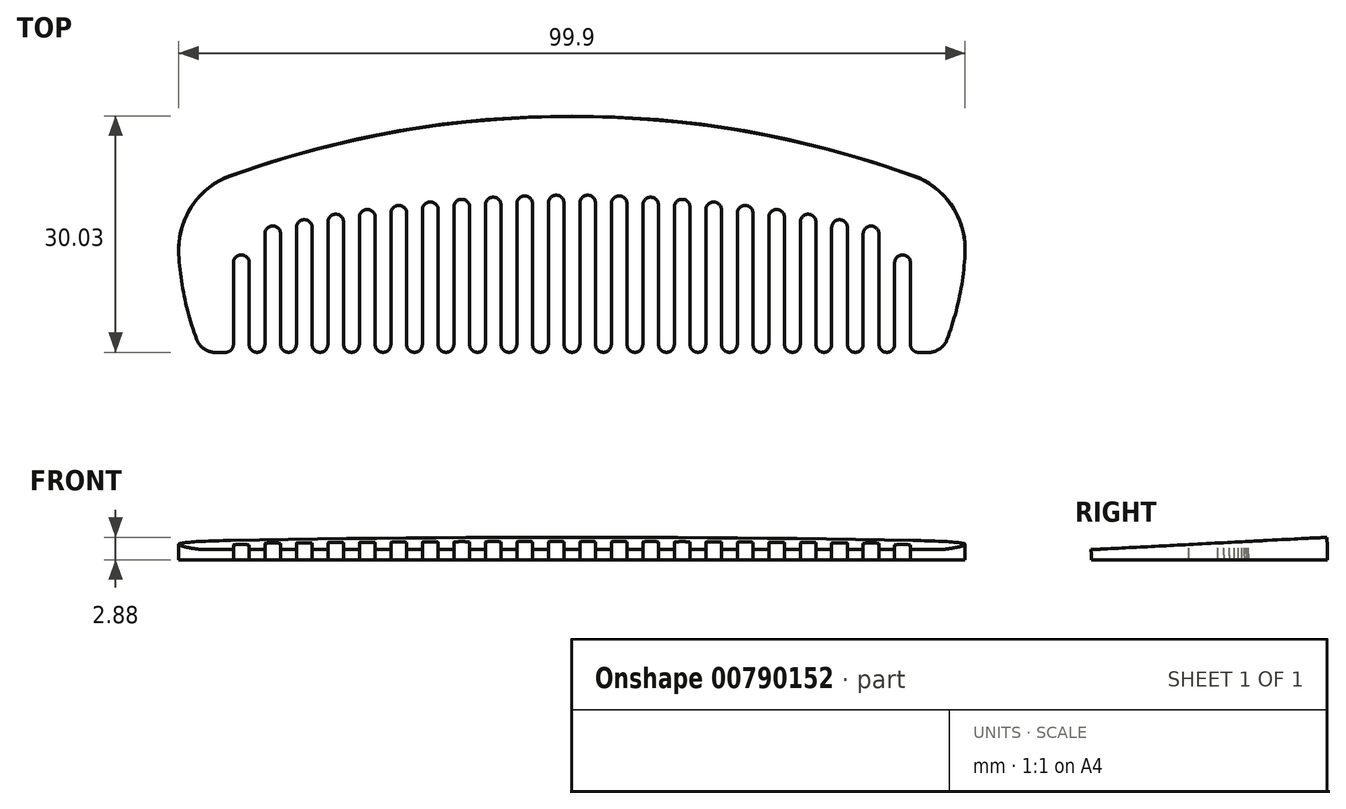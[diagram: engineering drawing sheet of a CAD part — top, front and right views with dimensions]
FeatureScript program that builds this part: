
annotation { "Feature Type Name" : "Feature", "Feature Type Description" : "" }
export const myFeature = defineFeature(function(context is Context, id is Id, definition is map)
    precondition{}
    {
        {
            var Q0;
            Q0=qCreatedBy(makeId("Top.planeOp"),FACE);
            var sketch = newSketch(context, id + "F0", { "sketchPlane" : qUnion([Q0])});
            skArc(sketch, "E0", {"start": v(-43.34, -7.56) * mm, "mid": v(-48.3, -11.46) * mm, "end": v(-49.94, -17.55) * mm});
            skArc(sketch, "E1", {"start": v(-49.94, -17.55) * mm, "mid": v(-49.01, -23.9) * mm, "end": v(-47, -30) * mm});
            skLineSegment(sketch, "E2", {"start": v(-47, -30) * mm, "end": v(-43, -30) * mm});
            skLineSegment(sketch, "E3", {"start": v(-43, -30) * mm, "end": v(-43, -18.6) * mm});
            skLineSegment(sketch, "E4", {"start": v(0, 0) * mm, "end": v(0, -30) * mm});
            skPoint(sketch, "E5", {"position": v(0, -10) * mm});
            skLineSegment(sketch, "E6", {"start": v(-41, -10) * mm, "end": v(-41, -30) * mm});
            skLineSegment(sketch, "E7", {"start": v(-41, -30) * mm, "end": v(-39, -30) * mm});
            skLineSegment(sketch, "E8", {"start": v(-39, -30) * mm, "end": v(-39, -10) * mm});
            skLineSegment(sketch, "E9", {"start": v(-39, -30) * mm, "end": v(-37, -30) * mm, "construction": true});
            skLineSegment(sketch, "E10", {"start": v(-43, -30) * mm, "end": v(-41, -30) * mm, "construction": true});
            skLineSegment(sketch, "E11", {"start": v(-47, -55) * mm, "end": v(0, -55) * mm, "construction": true});
            skArc(sketch, "E12", {"start": v(0, -10) * mm, "mid": v(-19.84, -11.05) * mm, "end": v(-39.45, -14.2) * mm});
            skLineSegment(sketch, "E13.1.0.0", {"start": v(-37, -10) * mm, "end": v(-37, -30) * mm});
            skLineSegment(sketch, "E13.1.0.1", {"start": v(-37, -30) * mm, "end": v(-35, -30) * mm});
            skLineSegment(sketch, "E13.1.0.2", {"start": v(-35, -30) * mm, "end": v(-35, -10) * mm});
            skLineSegment(sketch, "E13.1.0.3", {"start": v(-35, -30) * mm, "end": v(-33, -30) * mm, "construction": true});
            skLineSegment(sketch, "E13.2.0.0", {"start": v(-33, -10) * mm, "end": v(-33, -30) * mm});
            skLineSegment(sketch, "E13.2.0.1", {"start": v(-33, -30) * mm, "end": v(-31, -30) * mm});
            skLineSegment(sketch, "E13.2.0.2", {"start": v(-31, -30) * mm, "end": v(-31, -10) * mm});
            skLineSegment(sketch, "E13.2.0.3", {"start": v(-31, -30) * mm, "end": v(-29, -30) * mm, "construction": true});
            skLineSegment(sketch, "E13.direction1", {"start": v(-41, -30) * mm, "end": v(-37, -30) * mm, "construction": true});
            skLineSegment(sketch, "E14.0.3.0", {"start": v(-29, -10) * mm, "end": v(-29, -30) * mm});
            skLineSegment(sketch, "E14.3.3.0", {"start": v(-29, -30) * mm, "end": v(-27, -30) * mm});
            skLineSegment(sketch, "E14.6.3.0", {"start": v(-27, -30) * mm, "end": v(-27, -10) * mm});
            skLineSegment(sketch, "E14.9.3.0", {"start": v(-27, -30) * mm, "end": v(-25, -30) * mm, "construction": true});
            skLineSegment(sketch, "E14.0.4.0", {"start": v(-25, -10) * mm, "end": v(-25, -30) * mm});
            skLineSegment(sketch, "E14.3.4.0", {"start": v(-25, -30) * mm, "end": v(-23, -30) * mm});
            skLineSegment(sketch, "E14.6.4.0", {"start": v(-23, -30) * mm, "end": v(-23, -10) * mm});
            skLineSegment(sketch, "E14.9.4.0", {"start": v(-23, -30) * mm, "end": v(-21, -30) * mm, "construction": true});
            skLineSegment(sketch, "E14.0.5.0", {"start": v(-21, -10) * mm, "end": v(-21, -30) * mm});
            skLineSegment(sketch, "E14.3.5.0", {"start": v(-21, -30) * mm, "end": v(-19, -30) * mm});
            skLineSegment(sketch, "E14.6.5.0", {"start": v(-19, -30) * mm, "end": v(-19, -10) * mm});
            skLineSegment(sketch, "E14.9.5.0", {"start": v(-19, -30) * mm, "end": v(-17, -30) * mm, "construction": true});
            skLineSegment(sketch, "E14.0.6.0", {"start": v(-17, -10) * mm, "end": v(-17, -30) * mm});
            skLineSegment(sketch, "E14.3.6.0", {"start": v(-17, -30) * mm, "end": v(-15, -30) * mm});
            skLineSegment(sketch, "E14.6.6.0", {"start": v(-15, -30) * mm, "end": v(-15, -10) * mm});
            skLineSegment(sketch, "E14.9.6.0", {"start": v(-15, -30) * mm, "end": v(-13, -30) * mm, "construction": true});
            skLineSegment(sketch, "E14.0.7.0", {"start": v(-13, -10) * mm, "end": v(-13, -30) * mm});
            skLineSegment(sketch, "E14.3.7.0", {"start": v(-13, -30) * mm, "end": v(-11, -30) * mm});
            skLineSegment(sketch, "E14.6.7.0", {"start": v(-11, -30) * mm, "end": v(-11, -10) * mm});
            skLineSegment(sketch, "E14.9.7.0", {"start": v(-11, -30) * mm, "end": v(-9, -30) * mm, "construction": true});
            skLineSegment(sketch, "E14.0.8.0", {"start": v(-9, -10) * mm, "end": v(-9, -30) * mm});
            skLineSegment(sketch, "E14.3.8.0", {"start": v(-9, -30) * mm, "end": v(-7, -30) * mm});
            skLineSegment(sketch, "E14.6.8.0", {"start": v(-7, -30) * mm, "end": v(-7, -10) * mm});
            skLineSegment(sketch, "E14.9.8.0", {"start": v(-7, -30) * mm, "end": v(-5, -30) * mm, "construction": true});
            skLineSegment(sketch, "E14.0.9.0", {"start": v(-5, -10) * mm, "end": v(-5, -30) * mm});
            skLineSegment(sketch, "E14.3.9.0", {"start": v(-5, -30) * mm, "end": v(-3, -30) * mm});
            skLineSegment(sketch, "E14.6.9.0", {"start": v(-3, -30) * mm, "end": v(-3, -10) * mm});
            skLineSegment(sketch, "E14.9.9.0", {"start": v(-3, -30) * mm, "end": v(-1, -30) * mm, "construction": true});
            skArc(sketch, "E15", {"start": v(0, 0) * mm, "mid": v(-22, -1.9) * mm, "end": v(-43.34, -7.56) * mm});
            skArc(sketch, "E16", {"start": v(-39.45, -14.2) * mm, "mid": v(-42, -15.77) * mm, "end": v(-43, -18.6) * mm});
            skArc(sketch, "E17", {"start": v(-43.34, -7.56) * mm, "mid": v(-46.49, -8.74) * mm, "end": v(-49.6, -10) * mm, "construction": true});
            skArc(sketch, "E18", {"start": v(-49.6, -10) * mm, "mid": v(-49.96, -13.77) * mm, "end": v(-49.94, -17.55) * mm, "construction": true});
            skLineSegment(sketch, "E19", {"start": v(-43, -18.6) * mm, "end": v(-43, -15) * mm, "construction": true});
            skLineSegment(sketch, "E20", {"start": v(-50, 0) * mm, "end": v(-50, -30) * mm, "construction": true});
            skArc(sketch, "E21", {"start": v(-39.45, -14.2) * mm, "mid": v(-41.23, -14.6) * mm, "end": v(-43, -15) * mm, "construction": true});
            skLineSegment(sketch, "E22", {"start": v(0, -10) * mm, "end": v(-50, -10) * mm, "construction": true});
            skLineSegment(sketch, "E23", {"start": v(-50, 0) * mm, "end": v(0, 0) * mm, "construction": true});
            skLineSegment(sketch, "E24.0.10.0", {"start": v(-1, -10) * mm, "end": v(-1, -30) * mm});
            skLineSegment(sketch, "E24.3.10.0", {"start": v(-1, -30) * mm, "end": v(1, -30) * mm});
            skLineSegment(sketch, "E24.6.10.0", {"start": v(1, -30) * mm, "end": v(1, -10) * mm});
            skLineSegment(sketch, "E24.9.10.0", {"start": v(1, -30) * mm, "end": v(3, -30) * mm, "construction": true});
            skSolve(sketch);
        }
        {
            var Q0;
            Q0 = qSketchRegion(id + "F0", true);
            var Q1;
            Q1=sQuery(id+"F0.wireOp",EDGE,"E11");
            revolve(context, id + "F1", {"surfaceOperationType" : NewSurfaceOperationType.NEW, "entities" : qUnion([Q0]), "axis" : qUnion([Q1]), "revolveType" : RevolveType.ONE_DIRECTION, "angle" : 3 * degree});
        }
        {
            var Q0;
            Q0=makeQuery(id+"F1.opRevolve","SWEPT_EDGE",EDGE,{"disambiguationData":[OSD([sQuery(id+"F0.wireOp",EDGE,"E3"),sQuery(id+"F0.wireOp",EDGE,"E16")])]});
            var Q1;
            Q1=makeQuery(id+"F1.opRevolve","SWEPT_EDGE",EDGE,{"disambiguationData":[OSD([sQuery(id+"F0.wireOp",EDGE,"E6"),sQuery(id+"F0.wireOp",EDGE,"E16")])]});
            var Q2;
            Q2=makeQuery(id+"F1.opRevolve","SWEPT_EDGE",EDGE,{"disambiguationData":[OSD([sQuery(id+"F0.wireOp",EDGE,"E12"),sQuery(id+"F0.wireOp",EDGE,"E13.1.0.0")])]});
            var Q3;
            Q3=makeQuery(id+"F1.opRevolve","SWEPT_EDGE",EDGE,{"disambiguationData":[OSD([sQuery(id+"F0.wireOp",EDGE,"E8"),sQuery(id+"F0.wireOp",EDGE,"E12")])]});
            var Q4;
            Q4=makeQuery(id+"F1.opRevolve","SWEPT_EDGE",EDGE,{"disambiguationData":[OSD([sQuery(id+"F0.wireOp",EDGE,"E12"),sQuery(id+"F0.wireOp",EDGE,"E24.0.10.0")])]});
            var Q5;
            Q5=makeQuery(id+"F1.opRevolve","SWEPT_EDGE",EDGE,{"disambiguationData":[OSD([sQuery(id+"F0.wireOp",EDGE,"E12"),sQuery(id+"F0.wireOp",EDGE,"E14.6.9.0")])]});
            var Q6;
            Q6=makeQuery(id+"F1.opRevolve","SWEPT_EDGE",EDGE,{"disambiguationData":[OSD([sQuery(id+"F0.wireOp",EDGE,"E12"),sQuery(id+"F0.wireOp",EDGE,"E14.0.9.0")])]});
            var Q7;
            Q7=makeQuery(id+"F1.opRevolve","SWEPT_EDGE",EDGE,{"disambiguationData":[OSD([sQuery(id+"F0.wireOp",EDGE,"E12"),sQuery(id+"F0.wireOp",EDGE,"E14.6.8.0")])]});
            var Q8;
            Q8=makeQuery(id+"F1.opRevolve","SWEPT_EDGE",EDGE,{"disambiguationData":[OSD([sQuery(id+"F0.wireOp",EDGE,"E12"),sQuery(id+"F0.wireOp",EDGE,"E14.0.8.0")])]});
            var Q9;
            Q9=makeQuery(id+"F1.opRevolve","SWEPT_EDGE",EDGE,{"disambiguationData":[OSD([sQuery(id+"F0.wireOp",EDGE,"E12"),sQuery(id+"F0.wireOp",EDGE,"E14.6.7.0")])]});
            var Q10;
            Q10=makeQuery(id+"F1.opRevolve","SWEPT_EDGE",EDGE,{"disambiguationData":[OSD([sQuery(id+"F0.wireOp",EDGE,"E12"),sQuery(id+"F0.wireOp",EDGE,"E14.0.7.0")])]});
            var Q11;
            Q11=makeQuery(id+"F1.opRevolve","SWEPT_EDGE",EDGE,{"disambiguationData":[OSD([sQuery(id+"F0.wireOp",EDGE,"E12"),sQuery(id+"F0.wireOp",EDGE,"E14.6.6.0")])]});
            var Q12;
            Q12=makeQuery(id+"F1.opRevolve","SWEPT_EDGE",EDGE,{"disambiguationData":[OSD([sQuery(id+"F0.wireOp",EDGE,"E12"),sQuery(id+"F0.wireOp",EDGE,"E14.0.6.0")])]});
            var Q13;
            Q13=makeQuery(id+"F1.opRevolve","SWEPT_EDGE",EDGE,{"disambiguationData":[OSD([sQuery(id+"F0.wireOp",EDGE,"E12"),sQuery(id+"F0.wireOp",EDGE,"E14.6.5.0")])]});
            var Q14;
            Q14=makeQuery(id+"F1.opRevolve","SWEPT_EDGE",EDGE,{"disambiguationData":[OSD([sQuery(id+"F0.wireOp",EDGE,"E12"),sQuery(id+"F0.wireOp",EDGE,"E14.0.5.0")])]});
            var Q15;
            Q15=makeQuery(id+"F1.opRevolve","SWEPT_EDGE",EDGE,{"disambiguationData":[OSD([sQuery(id+"F0.wireOp",EDGE,"E12"),sQuery(id+"F0.wireOp",EDGE,"E14.6.4.0")])]});
            var Q16;
            Q16=makeQuery(id+"F1.opRevolve","SWEPT_EDGE",EDGE,{"disambiguationData":[OSD([sQuery(id+"F0.wireOp",EDGE,"E12"),sQuery(id+"F0.wireOp",EDGE,"E14.0.4.0")])]});
            var Q17;
            Q17=makeQuery(id+"F1.opRevolve","SWEPT_EDGE",EDGE,{"disambiguationData":[OSD([sQuery(id+"F0.wireOp",EDGE,"E12"),sQuery(id+"F0.wireOp",EDGE,"E14.6.3.0")])]});
            var Q18;
            Q18=makeQuery(id+"F1.opRevolve","SWEPT_EDGE",EDGE,{"disambiguationData":[OSD([sQuery(id+"F0.wireOp",EDGE,"E12"),sQuery(id+"F0.wireOp",EDGE,"E14.0.3.0")])]});
            var Q19;
            Q19=makeQuery(id+"F1.opRevolve","SWEPT_EDGE",EDGE,{"disambiguationData":[OSD([sQuery(id+"F0.wireOp",EDGE,"E12"),sQuery(id+"F0.wireOp",EDGE,"E13.2.0.2")])]});
            var Q20;
            Q20=makeQuery(id+"F1.opRevolve","SWEPT_EDGE",EDGE,{"disambiguationData":[OSD([sQuery(id+"F0.wireOp",EDGE,"E12"),sQuery(id+"F0.wireOp",EDGE,"E13.2.0.0")])]});
            var Q21;
            Q21=makeQuery(id+"F1.opRevolve","SWEPT_EDGE",EDGE,{"disambiguationData":[OSD([sQuery(id+"F0.wireOp",EDGE,"E12"),sQuery(id+"F0.wireOp",EDGE,"E13.1.0.2")])]});
            fillet(context, id + "F2", {"entities" : qUnion([Q0, Q1, Q2, Q3, Q4, Q5, Q6, Q7, Q8, Q9, Q10, Q11, Q12, Q13, Q14, Q15, Q16, Q17, Q18, Q19, Q20, Q21]), "radius" : 1 * mm, "tangentPropagation" : true, "allowEdgeOverflow" : false});
        }
        {
            var Q0;
            Q0=makeQuery(id+"F1.opRevolve","SWEPT_EDGE",EDGE,{"disambiguationData":[OSD([sQuery(id+"F0.wireOp",EDGE,"E14.0.20.0"),sQuery(id+"F0.wireOp",EDGE,"E14.3.20.0")])]});
            var Q1;
            Q1=makeQuery(id+"F1.opRevolve","SWEPT_EDGE",EDGE,{"disambiguationData":[OSD([sQuery(id+"F0.wireOp",EDGE,"E14.3.20.0"),sQuery(id+"F0.wireOp",EDGE,"E14.6.20.0")])]});
            var Q2;
            Q2=makeQuery(id+"F1.opRevolve","SWEPT_EDGE",EDGE,{"disambiguationData":[OSD([sQuery(id+"F0.wireOp",EDGE,"E14.3.19.0"),sQuery(id+"F0.wireOp",EDGE,"E14.6.19.0")])]});
            var Q3;
            Q3=makeQuery(id+"F1.opRevolve","SWEPT_EDGE",EDGE,{"disambiguationData":[OSD([sQuery(id+"F0.wireOp",EDGE,"E14.0.19.0"),sQuery(id+"F0.wireOp",EDGE,"E14.3.19.0")])]});
            var Q4;
            Q4=makeQuery(id+"F1.opRevolve","SWEPT_EDGE",EDGE,{"disambiguationData":[OSD([sQuery(id+"F0.wireOp",EDGE,"E14.3.18.0"),sQuery(id+"F0.wireOp",EDGE,"E14.6.18.0")])]});
            var Q5;
            Q5=makeQuery(id+"F1.opRevolve","SWEPT_EDGE",EDGE,{"disambiguationData":[OSD([sQuery(id+"F0.wireOp",EDGE,"E14.0.18.0"),sQuery(id+"F0.wireOp",EDGE,"E14.3.18.0")])]});
            var Q6;
            Q6=makeQuery(id+"F1.opRevolve","SWEPT_EDGE",EDGE,{"disambiguationData":[OSD([sQuery(id+"F0.wireOp",EDGE,"E14.3.17.0"),sQuery(id+"F0.wireOp",EDGE,"E14.6.17.0")])]});
            var Q7;
            Q7=makeQuery(id+"F1.opRevolve","SWEPT_EDGE",EDGE,{"disambiguationData":[OSD([sQuery(id+"F0.wireOp",EDGE,"E14.0.17.0"),sQuery(id+"F0.wireOp",EDGE,"E14.3.17.0")])]});
            var Q8;
            Q8=makeQuery(id+"F1.opRevolve","SWEPT_EDGE",EDGE,{"disambiguationData":[OSD([sQuery(id+"F0.wireOp",EDGE,"E14.3.16.0"),sQuery(id+"F0.wireOp",EDGE,"E14.6.16.0")])]});
            var Q9;
            Q9=makeQuery(id+"F1.opRevolve","SWEPT_EDGE",EDGE,{"disambiguationData":[OSD([sQuery(id+"F0.wireOp",EDGE,"E14.0.16.0"),sQuery(id+"F0.wireOp",EDGE,"E14.3.16.0")])]});
            var Q10;
            Q10=makeQuery(id+"F1.opRevolve","SWEPT_EDGE",EDGE,{"disambiguationData":[OSD([sQuery(id+"F0.wireOp",EDGE,"E14.3.15.0"),sQuery(id+"F0.wireOp",EDGE,"E14.6.15.0")])]});
            var Q11;
            Q11=makeQuery(id+"F1.opRevolve","SWEPT_EDGE",EDGE,{"disambiguationData":[OSD([sQuery(id+"F0.wireOp",EDGE,"E14.0.15.0"),sQuery(id+"F0.wireOp",EDGE,"E14.3.15.0")])]});
            var Q12;
            Q12=makeQuery(id+"F1.opRevolve","SWEPT_EDGE",EDGE,{"disambiguationData":[OSD([sQuery(id+"F0.wireOp",EDGE,"E14.3.14.0"),sQuery(id+"F0.wireOp",EDGE,"E14.6.14.0")])]});
            var Q13;
            Q13=makeQuery(id+"F1.opRevolve","SWEPT_EDGE",EDGE,{"disambiguationData":[OSD([sQuery(id+"F0.wireOp",EDGE,"E14.0.14.0"),sQuery(id+"F0.wireOp",EDGE,"E14.3.14.0")])]});
            var Q14;
            Q14=makeQuery(id+"F1.opRevolve","SWEPT_EDGE",EDGE,{"disambiguationData":[OSD([sQuery(id+"F0.wireOp",EDGE,"E14.3.13.0"),sQuery(id+"F0.wireOp",EDGE,"E14.6.13.0")])]});
            var Q15;
            Q15=makeQuery(id+"F1.opRevolve","SWEPT_EDGE",EDGE,{"disambiguationData":[OSD([sQuery(id+"F0.wireOp",EDGE,"E14.0.13.0"),sQuery(id+"F0.wireOp",EDGE,"E14.3.13.0")])]});
            var Q16;
            Q16=makeQuery(id+"F1.opRevolve","SWEPT_EDGE",EDGE,{"disambiguationData":[OSD([sQuery(id+"F0.wireOp",EDGE,"E14.3.12.0"),sQuery(id+"F0.wireOp",EDGE,"E14.6.12.0")])]});
            var Q17;
            Q17=makeQuery(id+"F1.opRevolve","SWEPT_EDGE",EDGE,{"disambiguationData":[OSD([sQuery(id+"F0.wireOp",EDGE,"E14.0.12.0"),sQuery(id+"F0.wireOp",EDGE,"E14.3.12.0")])]});
            var Q18;
            Q18=makeQuery(id+"F1.opRevolve","SWEPT_EDGE",EDGE,{"disambiguationData":[OSD([sQuery(id+"F0.wireOp",EDGE,"E14.3.11.0"),sQuery(id+"F0.wireOp",EDGE,"E14.6.11.0")])]});
            var Q19;
            Q19=makeQuery(id+"F1.opRevolve","SWEPT_EDGE",EDGE,{"disambiguationData":[OSD([sQuery(id+"F0.wireOp",EDGE,"E14.0.11.0"),sQuery(id+"F0.wireOp",EDGE,"E14.3.11.0")])]});
            var Q20;
            Q20=makeQuery(id+"F1.opRevolve","SWEPT_EDGE",EDGE,{"disambiguationData":[OSD([sQuery(id+"F0.wireOp",EDGE,"E14.3.10.0"),sQuery(id+"F0.wireOp",EDGE,"E14.6.10.0")])]});
            var Q21;
            Q21=makeQuery(id+"F1.opRevolve","SWEPT_EDGE",EDGE,{"disambiguationData":[OSD([sQuery(id+"F0.wireOp",EDGE,"E14.0.10.0"),sQuery(id+"F0.wireOp",EDGE,"E14.3.10.0")])]});
            var Q22;
            Q22=makeQuery(id+"F1.opRevolve","SWEPT_EDGE",EDGE,{"disambiguationData":[OSD([sQuery(id+"F0.wireOp",EDGE,"E14.3.9.0"),sQuery(id+"F0.wireOp",EDGE,"E14.6.9.0")])]});
            var Q23;
            Q23=makeQuery(id+"F1.opRevolve","SWEPT_EDGE",EDGE,{"disambiguationData":[OSD([sQuery(id+"F0.wireOp",EDGE,"E14.0.9.0"),sQuery(id+"F0.wireOp",EDGE,"E14.3.9.0")])]});
            var Q24;
            Q24=makeQuery(id+"F1.opRevolve","SWEPT_EDGE",EDGE,{"disambiguationData":[OSD([sQuery(id+"F0.wireOp",EDGE,"E14.3.8.0"),sQuery(id+"F0.wireOp",EDGE,"E14.6.8.0")])]});
            var Q25;
            Q25=makeQuery(id+"F1.opRevolve","SWEPT_EDGE",EDGE,{"disambiguationData":[OSD([sQuery(id+"F0.wireOp",EDGE,"E14.0.8.0"),sQuery(id+"F0.wireOp",EDGE,"E14.3.8.0")])]});
            var Q26;
            Q26=makeQuery(id+"F1.opRevolve","SWEPT_EDGE",EDGE,{"disambiguationData":[OSD([sQuery(id+"F0.wireOp",EDGE,"E14.3.7.0"),sQuery(id+"F0.wireOp",EDGE,"E14.6.7.0")])]});
            var Q27;
            Q27=makeQuery(id+"F1.opRevolve","SWEPT_EDGE",EDGE,{"disambiguationData":[OSD([sQuery(id+"F0.wireOp",EDGE,"E14.0.7.0"),sQuery(id+"F0.wireOp",EDGE,"E14.3.7.0")])]});
            var Q28;
            Q28=makeQuery(id+"F1.opRevolve","SWEPT_EDGE",EDGE,{"disambiguationData":[OSD([sQuery(id+"F0.wireOp",EDGE,"E14.3.6.0"),sQuery(id+"F0.wireOp",EDGE,"E14.6.6.0")])]});
            var Q29;
            Q29=makeQuery(id+"F1.opRevolve","SWEPT_EDGE",EDGE,{"disambiguationData":[OSD([sQuery(id+"F0.wireOp",EDGE,"E14.0.6.0"),sQuery(id+"F0.wireOp",EDGE,"E14.3.6.0")])]});
            var Q30;
            Q30=makeQuery(id+"F1.opRevolve","SWEPT_EDGE",EDGE,{"disambiguationData":[OSD([sQuery(id+"F0.wireOp",EDGE,"E14.3.5.0"),sQuery(id+"F0.wireOp",EDGE,"E14.6.5.0")])]});
            var Q31;
            Q31=makeQuery(id+"F1.opRevolve","SWEPT_EDGE",EDGE,{"disambiguationData":[OSD([sQuery(id+"F0.wireOp",EDGE,"E14.0.5.0"),sQuery(id+"F0.wireOp",EDGE,"E14.3.5.0")])]});
            var Q32;
            Q32=makeQuery(id+"F1.opRevolve","SWEPT_EDGE",EDGE,{"disambiguationData":[OSD([sQuery(id+"F0.wireOp",EDGE,"E14.3.4.0"),sQuery(id+"F0.wireOp",EDGE,"E14.6.4.0")])]});
            var Q33;
            Q33=makeQuery(id+"F1.opRevolve","SWEPT_EDGE",EDGE,{"disambiguationData":[OSD([sQuery(id+"F0.wireOp",EDGE,"E14.0.4.0"),sQuery(id+"F0.wireOp",EDGE,"E14.3.4.0")])]});
            var Q34;
            Q34=makeQuery(id+"F1.opRevolve","SWEPT_EDGE",EDGE,{"disambiguationData":[OSD([sQuery(id+"F0.wireOp",EDGE,"E14.3.3.0"),sQuery(id+"F0.wireOp",EDGE,"E14.6.3.0")])]});
            var Q35;
            Q35=makeQuery(id+"F1.opRevolve","SWEPT_EDGE",EDGE,{"disambiguationData":[OSD([sQuery(id+"F0.wireOp",EDGE,"E14.0.3.0"),sQuery(id+"F0.wireOp",EDGE,"E14.3.3.0")])]});
            var Q36;
            Q36=makeQuery(id+"F1.opRevolve","SWEPT_EDGE",EDGE,{"disambiguationData":[OSD([sQuery(id+"F0.wireOp",EDGE,"E13.2.0.1"),sQuery(id+"F0.wireOp",EDGE,"E13.2.0.2")])]});
            var Q37;
            Q37=makeQuery(id+"F1.opRevolve","SWEPT_EDGE",EDGE,{"disambiguationData":[OSD([sQuery(id+"F0.wireOp",EDGE,"E13.2.0.0"),sQuery(id+"F0.wireOp",EDGE,"E13.2.0.1")])]});
            var Q38;
            Q38=makeQuery(id+"F1.opRevolve","SWEPT_EDGE",EDGE,{"disambiguationData":[OSD([sQuery(id+"F0.wireOp",EDGE,"E13.1.0.1"),sQuery(id+"F0.wireOp",EDGE,"E13.1.0.2")])]});
            var Q39;
            Q39=makeQuery(id+"F1.opRevolve","SWEPT_EDGE",EDGE,{"disambiguationData":[OSD([sQuery(id+"F0.wireOp",EDGE,"E13.1.0.0"),sQuery(id+"F0.wireOp",EDGE,"E13.1.0.1")])]});
            var Q40;
            Q40=makeQuery(id+"F1.opRevolve","SWEPT_EDGE",EDGE,{"disambiguationData":[OSD([sQuery(id+"F0.wireOp",EDGE,"E7"),sQuery(id+"F0.wireOp",EDGE,"E8")])]});
            var Q41;
            Q41=makeQuery(id+"F1.opRevolve","SWEPT_EDGE",EDGE,{"disambiguationData":[OSD([sQuery(id+"F0.wireOp",EDGE,"E6"),sQuery(id+"F0.wireOp",EDGE,"E7")])]});
            var Q42;
            Q42=makeQuery(id+"F1.opRevolve","SWEPT_EDGE",EDGE,{"disambiguationData":[OSD([sQuery(id+"F0.wireOp",EDGE,"E2"),sQuery(id+"F0.wireOp",EDGE,"E3")])]});
            var Q43;
            Q43=makeQuery(id+"F1.opRevolve","SWEPT_EDGE",EDGE,{"disambiguationData":[OSD([sQuery(id+"F0.wireOp",EDGE,"E24.0.10.0"),sQuery(id+"F0.wireOp",EDGE,"E24.3.10.0")])]});
            fillet(context, id + "F3", {"entities" : qUnion([Q0, Q1, Q2, Q3, Q4, Q5, Q6, Q7, Q8, Q9, Q10, Q11, Q12, Q13, Q14, Q15, Q16, Q17, Q18, Q19, Q20, Q21, Q22, Q23, Q24, Q25, Q26, Q27, Q28, Q29, Q30, Q31, Q32, Q33, Q34, Q35, Q36, Q37, Q38, Q39, Q40, Q41, Q42, Q43]), "radius" : 1 * mm, "tangentPropagation" : true, "allowEdgeOverflow" : false});
        }
        {
            var Q0;
            Q0=makeQuery(id+"F1.opRevolve","SWEPT_EDGE",EDGE,{"disambiguationData":[OSD([sQuery(id+"F0.wireOp",EDGE,"E1"),sQuery(id+"F0.wireOp",EDGE,"E2")])]});
            fillet(context, id + "F4", {"entities" : qUnion([Q0]), "radius" : 2.5 * mm, "tangentPropagation" : true, "allowEdgeOverflow" : false});
        }
        {
            var Q0;
            Q0=makeQuery(id+"F1.opRevolve","SWEPT_BODY",BODY,{"disambiguationData":[OSD([sQuery(id+"F0.wireOp",EDGE,"E0"),sQuery(id+"F0.wireOp",EDGE,"E1"),sQuery(id+"F0.wireOp",EDGE,"E2"),sQuery(id+"F0.wireOp",EDGE,"E3"),sQuery(id+"F0.wireOp",EDGE,"E4"),sQuery(id+"F0.wireOp",EDGE,"E6"),sQuery(id+"F0.wireOp",EDGE,"E7"),sQuery(id+"F0.wireOp",EDGE,"E8"),sQuery(id+"F0.wireOp",EDGE,"E12"),sQuery(id+"F0.wireOp",EDGE,"E13.1.0.0"),sQuery(id+"F0.wireOp",EDGE,"E13.1.0.1"),sQuery(id+"F0.wireOp",EDGE,"E13.1.0.2"),sQuery(id+"F0.wireOp",EDGE,"E13.2.0.0"),sQuery(id+"F0.wireOp",EDGE,"E13.2.0.1"),sQuery(id+"F0.wireOp",EDGE,"E13.2.0.2"),sQuery(id+"F0.wireOp",EDGE,"E14.0.3.0"),sQuery(id+"F0.wireOp",EDGE,"E14.3.3.0"),sQuery(id+"F0.wireOp",EDGE,"E14.6.3.0"),sQuery(id+"F0.wireOp",EDGE,"E14.0.4.0"),sQuery(id+"F0.wireOp",EDGE,"E14.3.4.0"),sQuery(id+"F0.wireOp",EDGE,"E14.6.4.0"),sQuery(id+"F0.wireOp",EDGE,"E14.0.5.0"),sQuery(id+"F0.wireOp",EDGE,"E14.3.5.0"),sQuery(id+"F0.wireOp",EDGE,"E14.6.5.0"),sQuery(id+"F0.wireOp",EDGE,"E14.0.6.0"),sQuery(id+"F0.wireOp",EDGE,"E14.3.6.0"),sQuery(id+"F0.wireOp",EDGE,"E14.6.6.0"),sQuery(id+"F0.wireOp",EDGE,"E14.0.7.0"),sQuery(id+"F0.wireOp",EDGE,"E14.3.7.0"),sQuery(id+"F0.wireOp",EDGE,"E14.6.7.0"),sQuery(id+"F0.wireOp",EDGE,"E14.0.8.0"),sQuery(id+"F0.wireOp",EDGE,"E14.3.8.0"),sQuery(id+"F0.wireOp",EDGE,"E14.6.8.0"),sQuery(id+"F0.wireOp",EDGE,"E14.0.9.0"),sQuery(id+"F0.wireOp",EDGE,"E14.3.9.0"),sQuery(id+"F0.wireOp",EDGE,"E14.6.9.0"),sQuery(id+"F0.wireOp",EDGE,"E14.0.10.0"),sQuery(id+"F0.wireOp",EDGE,"E14.3.10.0"),sQuery(id+"F0.wireOp",EDGE,"E14.6.10.0"),sQuery(id+"F0.wireOp",EDGE,"E14.0.11.0"),sQuery(id+"F0.wireOp",EDGE,"E14.3.11.0"),sQuery(id+"F0.wireOp",EDGE,"E14.6.11.0"),sQuery(id+"F0.wireOp",EDGE,"E14.0.12.0"),sQuery(id+"F0.wireOp",EDGE,"E14.3.12.0"),sQuery(id+"F0.wireOp",EDGE,"E14.6.12.0"),sQuery(id+"F0.wireOp",EDGE,"E14.0.13.0"),sQuery(id+"F0.wireOp",EDGE,"E14.3.13.0"),sQuery(id+"F0.wireOp",EDGE,"E14.6.13.0"),sQuery(id+"F0.wireOp",EDGE,"E14.0.14.0"),sQuery(id+"F0.wireOp",EDGE,"E14.3.14.0"),sQuery(id+"F0.wireOp",EDGE,"E14.6.14.0"),sQuery(id+"F0.wireOp",EDGE,"E14.0.15.0"),sQuery(id+"F0.wireOp",EDGE,"E14.3.15.0"),sQuery(id+"F0.wireOp",EDGE,"E14.6.15.0"),sQuery(id+"F0.wireOp",EDGE,"E14.0.16.0"),sQuery(id+"F0.wireOp",EDGE,"E14.3.16.0"),sQuery(id+"F0.wireOp",EDGE,"E14.6.16.0"),sQuery(id+"F0.wireOp",EDGE,"E14.0.17.0"),sQuery(id+"F0.wireOp",EDGE,"E14.3.17.0"),sQuery(id+"F0.wireOp",EDGE,"E14.6.17.0"),sQuery(id+"F0.wireOp",EDGE,"E14.0.18.0"),sQuery(id+"F0.wireOp",EDGE,"E14.3.18.0"),sQuery(id+"F0.wireOp",EDGE,"E14.6.18.0"),sQuery(id+"F0.wireOp",EDGE,"E14.0.19.0"),sQuery(id+"F0.wireOp",EDGE,"E14.3.19.0"),sQuery(id+"F0.wireOp",EDGE,"E14.6.19.0"),sQuery(id+"F0.wireOp",EDGE,"E14.0.20.0"),sQuery(id+"F0.wireOp",EDGE,"E14.3.20.0"),sQuery(id+"F0.wireOp",EDGE,"E14.6.20.0"),sQuery(id+"F0.wireOp",EDGE,"E15"),sQuery(id+"F0.wireOp",EDGE,"E16")])]});
            var Q1;
            Q1=makeQuery(id+"F1.opRevolve","SWEPT_FACE",FACE,{"disambiguationData":[OSD([sQuery(id+"F0.wireOp",EDGE,"E4")])]});
            mirror(context, id + "F5", {"operationType" : NewBodyOperationType.ADD, "entities" : qUnion([Q0]), "mirrorPlane" : qUnion([Q1])});
        }
    });
